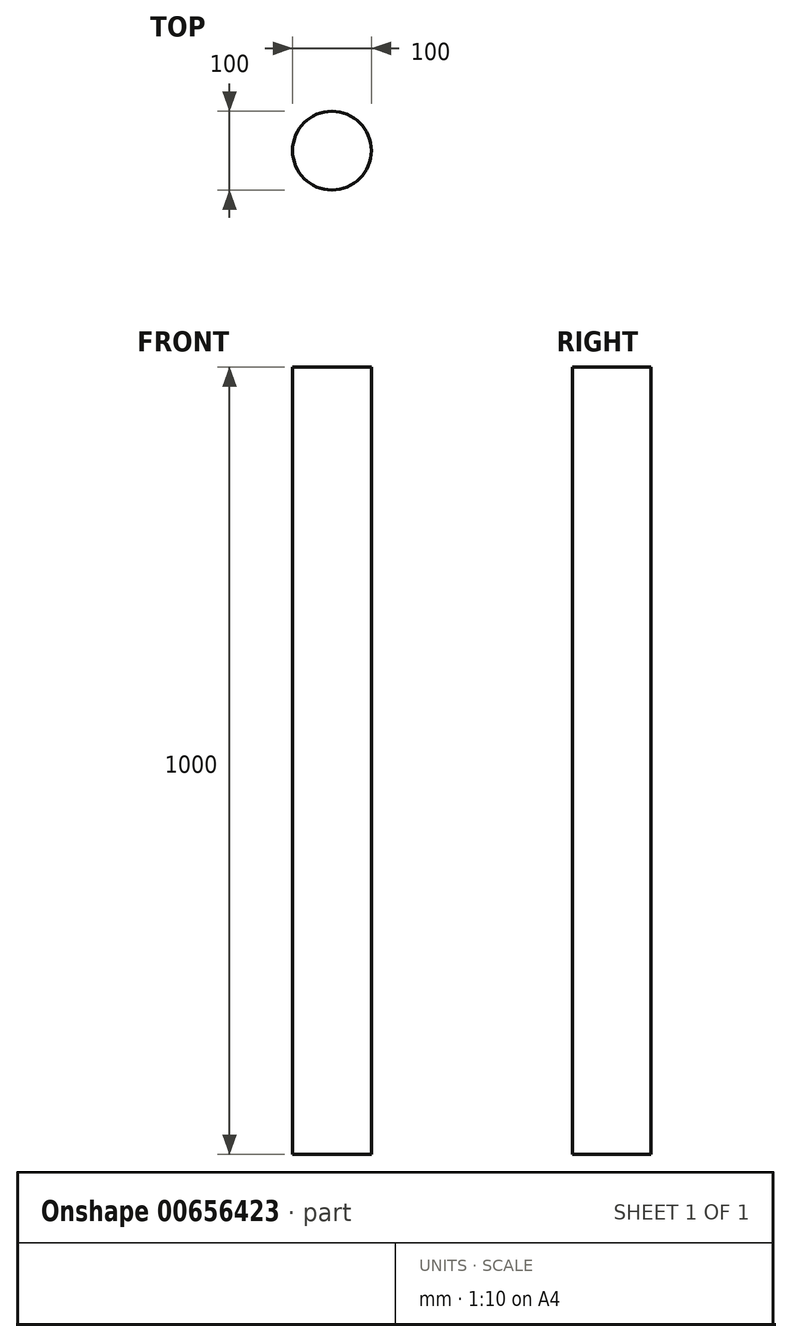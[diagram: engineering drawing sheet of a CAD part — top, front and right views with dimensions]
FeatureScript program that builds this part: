
annotation { "Feature Type Name" : "Feature", "Feature Type Description" : "" }
export const myFeature = defineFeature(function(context is Context, id is Id, definition is map)
    precondition{}
    {
        {
            var Q0;
            Q0=qCreatedBy(makeId("Top.planeOp"),FACE);
            var sketch = newSketch(context, id + "F0", { "sketchPlane" : qUnion([Q0])});
            skCircle(sketch, "E0", {"center": v(0, 0) * mm, "radius": 50 * mm});
            skSolve(sketch);
        }
        {
            var Q0;
            Q0=makeQuery(id+"F0.imprint","IMPRINT",FACE,{"disambiguationData":[TD([[makeQuery(id+"F0.imprint","IMPRINT",EDGE,{"derivedFrom":sQuery(id+"F0.wireOp",EDGE,"E0")}),1.0]])]});
            extrude(context, id + "F1", {"entities" : qUnion([Q0]), "depth" : 1000 * mm, "offsetDistance" : 25 * mm});
        }
    });
